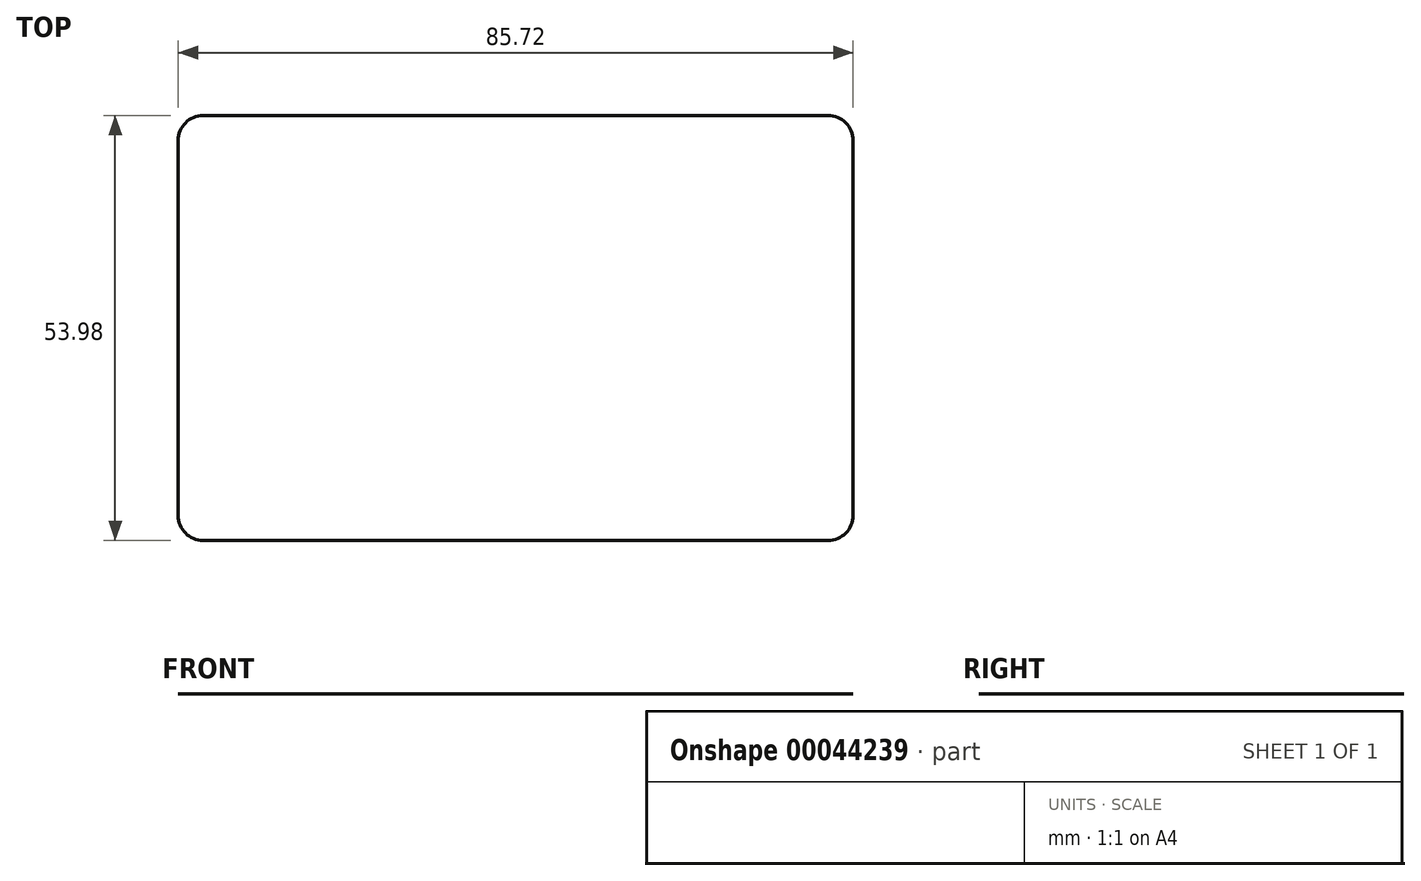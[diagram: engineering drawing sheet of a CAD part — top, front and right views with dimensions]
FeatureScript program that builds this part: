
annotation { "Feature Type Name" : "Feature", "Feature Type Description" : "" }
export const myFeature = defineFeature(function(context is Context, id is Id, definition is map)
    precondition{}
    {
        {
            var Q0;
            Q0=qCreatedBy(makeId("Top.planeOp"),FACE);
            var sketch = newSketch(context, id + "F0", { "sketchPlane" : qUnion([Q0])});
            skLineSegment(sketch, "E0.rect.bottom", {"start": v(39.69, 26.99) * mm, "end": v(-39.69, 26.99) * mm});
            skLineSegment(sketch, "E0.rect.top", {"start": v(39.69, -26.99) * mm, "end": v(-39.69, -26.99) * mm});
            skLineSegment(sketch, "E0.rect.left", {"start": v(42.86, 23.81) * mm, "end": v(42.86, -23.81) * mm});
            skLineSegment(sketch, "E0.rect.right", {"start": v(-42.86, 23.81) * mm, "end": v(-42.86, -23.81) * mm});
            skPoint(sketch, "E0.rect.middle", {"position": v(0, 0) * mm});
            skPoint(sketch, "E1.visualSharp", {"position": v(-42.86, 26.99) * mm});
            skArc(sketch, "E1.filletArc", {"start": v(-39.69, 26.99) * mm, "mid": v(-41.93, 26.06) * mm, "end": v(-42.86, 23.81) * mm});
            skPoint(sketch, "E2.visualSharp", {"position": v(-42.86, -26.99) * mm});
            skArc(sketch, "E2.filletArc", {"start": v(-42.86, -23.81) * mm, "mid": v(-41.93, -26.06) * mm, "end": v(-39.69, -26.99) * mm});
            skPoint(sketch, "E3.visualSharp", {"position": v(42.86, -26.99) * mm});
            skArc(sketch, "E3.filletArc", {"start": v(39.69, -26.99) * mm, "mid": v(41.93, -26.06) * mm, "end": v(42.86, -23.81) * mm});
            skPoint(sketch, "E4.visualSharp", {"position": v(42.86, 26.99) * mm});
            skArc(sketch, "E4.filletArc", {"start": v(42.86, 23.81) * mm, "mid": v(41.93, 26.06) * mm, "end": v(39.69, 26.99) * mm});
            skSolve(sketch);
        }
        {
            var Q0;
            Q0=makeQuery(id+"F0.imprint","IMPRINT",FACE,{"disambiguationData":[TD([[makeQuery(id+"F0.imprint","IMPRINT",EDGE,{"derivedFrom":sQuery(id+"F0.wireOp",EDGE,"E0.rect.bottom")}),1.0]])]});
            extrude(context, id + "F1", {"entities" : qUnion([Q0]), "depth" : 1 / 812.8 * mm});
        }
    });
